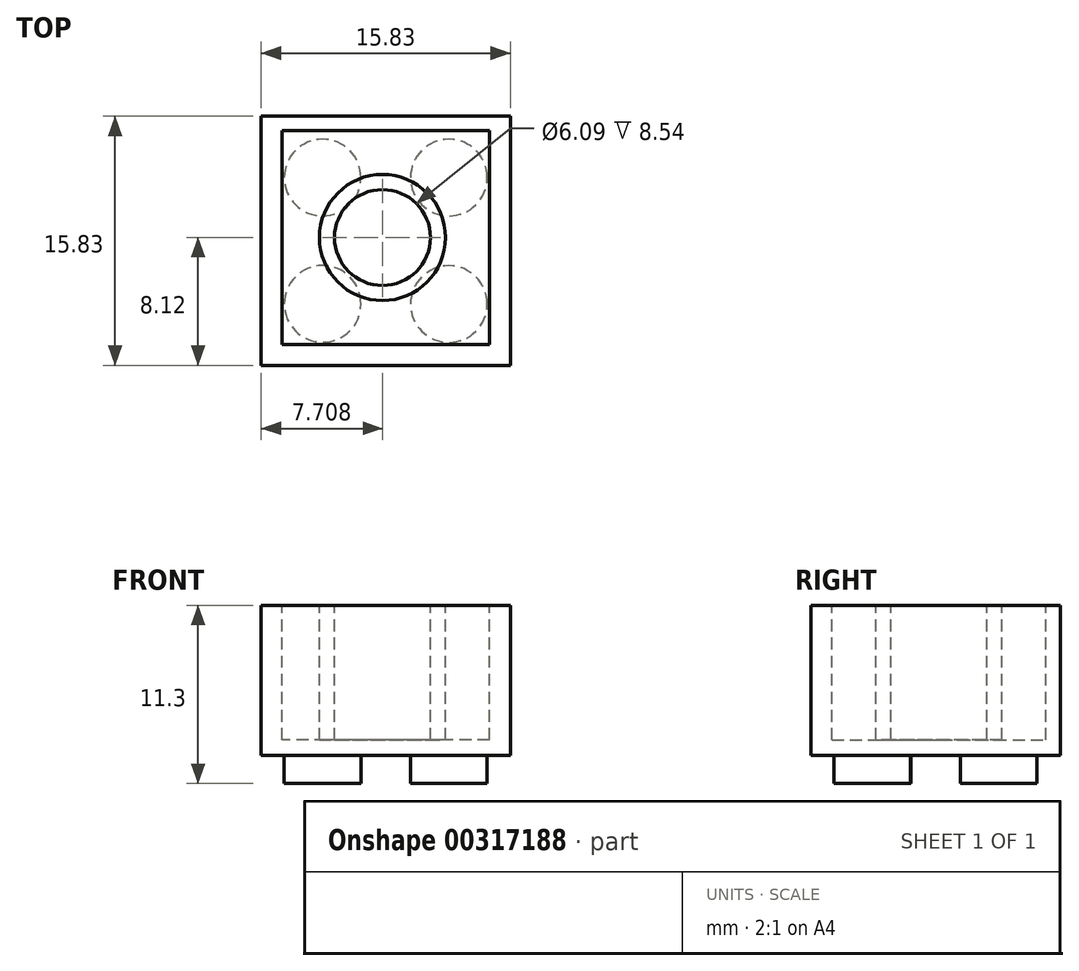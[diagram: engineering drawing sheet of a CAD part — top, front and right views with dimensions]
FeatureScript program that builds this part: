
annotation { "Feature Type Name" : "Feature", "Feature Type Description" : "" }
export const myFeature = defineFeature(function(context is Context, id is Id, definition is map)
    precondition{}
    {
        {
            var Q0;
            Q0=qCreatedBy(makeId("Top.planeOp"),FACE);
            var sketch = newSketch(context, id + "F0", { "sketchPlane" : qUnion([Q0])});
            skLineSegment(sketch, "E0.bottom", {"start": v(-7.93, 7.71) * mm, "end": v(7.9, 7.71) * mm});
            skLineSegment(sketch, "E0.top", {"start": v(-7.93, -8.12) * mm, "end": v(7.9, -8.12) * mm});
            skLineSegment(sketch, "E0.left", {"start": v(-7.93, 7.71) * mm, "end": v(-7.93, -8.12) * mm});
            skLineSegment(sketch, "E0.right", {"start": v(7.9, 7.71) * mm, "end": v(7.9, -8.12) * mm});
            skCircle(sketch, "E1", {"center": v(-4.03, 3.8) * mm, "radius": 2.44 * mm});
            skCircle(sketch, "E2.1.0.0", {"center": v(4, 3.8) * mm, "radius": 2.44 * mm});
            skLineSegment(sketch, "E2.direction1", {"start": v(-4.03, 3.8) * mm, "end": v(4, 3.8) * mm, "construction": true});
            skCircle(sketch, "E3", {"center": v(-4.03, -4.21) * mm, "radius": 2.44 * mm});
            skCircle(sketch, "E4.1.0.0", {"center": v(4, -4.23) * mm, "radius": 2.44 * mm});
            skLineSegment(sketch, "E4.direction1", {"start": v(-4.03, -4.21) * mm, "end": v(4, -4.23) * mm, "construction": true});
            skSolve(sketch);
        }
        {
            var Q0;
            Q0=makeQuery(id+"F0.imprint","IMPRINT",FACE,{"disambiguationData":[TD([[makeQuery(id+"F0.imprint","IMPRINT",EDGE,{"derivedFrom":sQuery(id+"F0.wireOp",EDGE,"E3")}),1.0]])]});
            var Q1;
            Q1=makeQuery(id+"F0.imprint","IMPRINT",FACE,{"disambiguationData":[TD([[makeQuery(id+"F0.imprint","IMPRINT",EDGE,{"derivedFrom":sQuery(id+"F0.wireOp",EDGE,"E0.bottom")}),-1.0]])]});
            var Q2;
            Q2=makeQuery(id+"F0.imprint","IMPRINT",FACE,{"disambiguationData":[TD([[makeQuery(id+"F0.imprint","IMPRINT",EDGE,{"derivedFrom":sQuery(id+"F0.wireOp",EDGE,"E4.1.0.0")}),1.0]])]});
            var Q3;
            Q3=makeQuery(id+"F0.imprint","IMPRINT",FACE,{"disambiguationData":[TD([[makeQuery(id+"F0.imprint","IMPRINT",EDGE,{"derivedFrom":sQuery(id+"F0.wireOp",EDGE,"E2.1.0.0")}),1.0]])]});
            var Q4;
            Q4=makeQuery(id+"F0.imprint","IMPRINT",FACE,{"disambiguationData":[TD([[makeQuery(id+"F0.imprint","IMPRINT",EDGE,{"derivedFrom":sQuery(id+"F0.wireOp",EDGE,"E1")}),1.0]])]});
            extrude(context, id + "F1", {"entities" : qUnion([Q0, Q1, Q2, Q3, Q4]), "depth" : 9.53 * mm});
        }
        {
            var Q0;
            Q0=makeQuery(id+"F0.imprint","IMPRINT",FACE,{"disambiguationData":[TD([[makeQuery(id+"F0.imprint","IMPRINT",EDGE,{"derivedFrom":sQuery(id+"F0.wireOp",EDGE,"E3")}),1.0]])]});
            var Q1;
            Q1=makeQuery(id+"F0.imprint","IMPRINT",FACE,{"disambiguationData":[TD([[makeQuery(id+"F0.imprint","IMPRINT",EDGE,{"derivedFrom":sQuery(id+"F0.wireOp",EDGE,"E4.1.0.0")}),1.0]])]});
            var Q2;
            Q2=makeQuery(id+"F0.imprint","IMPRINT",FACE,{"disambiguationData":[TD([[makeQuery(id+"F0.imprint","IMPRINT",EDGE,{"derivedFrom":sQuery(id+"F0.wireOp",EDGE,"E1")}),1.0]])]});
            var Q3;
            Q3=makeQuery(id+"F0.imprint","IMPRINT",FACE,{"disambiguationData":[TD([[makeQuery(id+"F0.imprint","IMPRINT",EDGE,{"derivedFrom":sQuery(id+"F0.wireOp",EDGE,"E2.1.0.0")}),1.0]])]});
            extrude(context, id + "F2", {"entities" : qUnion([Q0, Q1, Q2, Q3]), "operationType" : NewBodyOperationType.ADD, "oppositeDirection" : true, "depth" : 1.77 * mm});
        }
        {
            var Q0;
            Q0=makeQuery(id+"F1.opExtrude","CAP_FACE",FACE,{"disambiguationData":[OSD([sQuery(id+"F0.wireOp",EDGE,"E0.bottom"),sQuery(id+"F0.wireOp",EDGE,"E0.top"),sQuery(id+"F0.wireOp",EDGE,"E0.left"),sQuery(id+"F0.wireOp",EDGE,"E0.right")])],"isStart":false});
            var sketch = newSketch(context, id + "F3", { "sketchPlane" : qUnion([Q0])});
            skCircle(sketch, "E5", {"center": v(-0.22, 0) * mm, "radius": 4 * mm});
            skLineSegment(sketch, "E6.bottom", {"start": v(6.57, -6.79) * mm, "end": v(-6.6, -6.79) * mm});
            skLineSegment(sketch, "E6.top", {"start": v(6.57, 6.79) * mm, "end": v(-6.6, 6.79) * mm});
            skLineSegment(sketch, "E6.left", {"start": v(6.57, -6.79) * mm, "end": v(6.57, 6.79) * mm});
            skLineSegment(sketch, "E6.right", {"start": v(-6.6, -6.79) * mm, "end": v(-6.6, 6.79) * mm});
            skPoint(sketch, "E6.middle", {"position": v(-0.02, 0) * mm});
            skCircle(sketch, "E7", {"center": v(-0.22, 0) * mm, "radius": 3.05 * mm});
            skSolve(sketch);
        }
        {
            var Q0;
            Q0=makeQuery(id+"F3.imprint","IMPRINT",FACE,{"disambiguationData":[TD([[makeQuery(id+"F3.imprint","IMPRINT",EDGE,{"derivedFrom":sQuery(id+"F3.wireOp",EDGE,"E5")}),-1.0]])]});
            var Q1;
            Q1=makeQuery(id+"F3.imprint","IMPRINT",FACE,{"disambiguationData":[TD([[makeQuery(id+"F3.imprint","IMPRINT",EDGE,{"derivedFrom":sQuery(id+"F3.wireOp",EDGE,"E7")}),1.0]])]});
            extrude(context, id + "F4", {"entities" : qUnion([Q0, Q1]), "operationType" : NewBodyOperationType.REMOVE, "oppositeDirection" : true, "depth" : 8.54 * mm});
        }
    });
